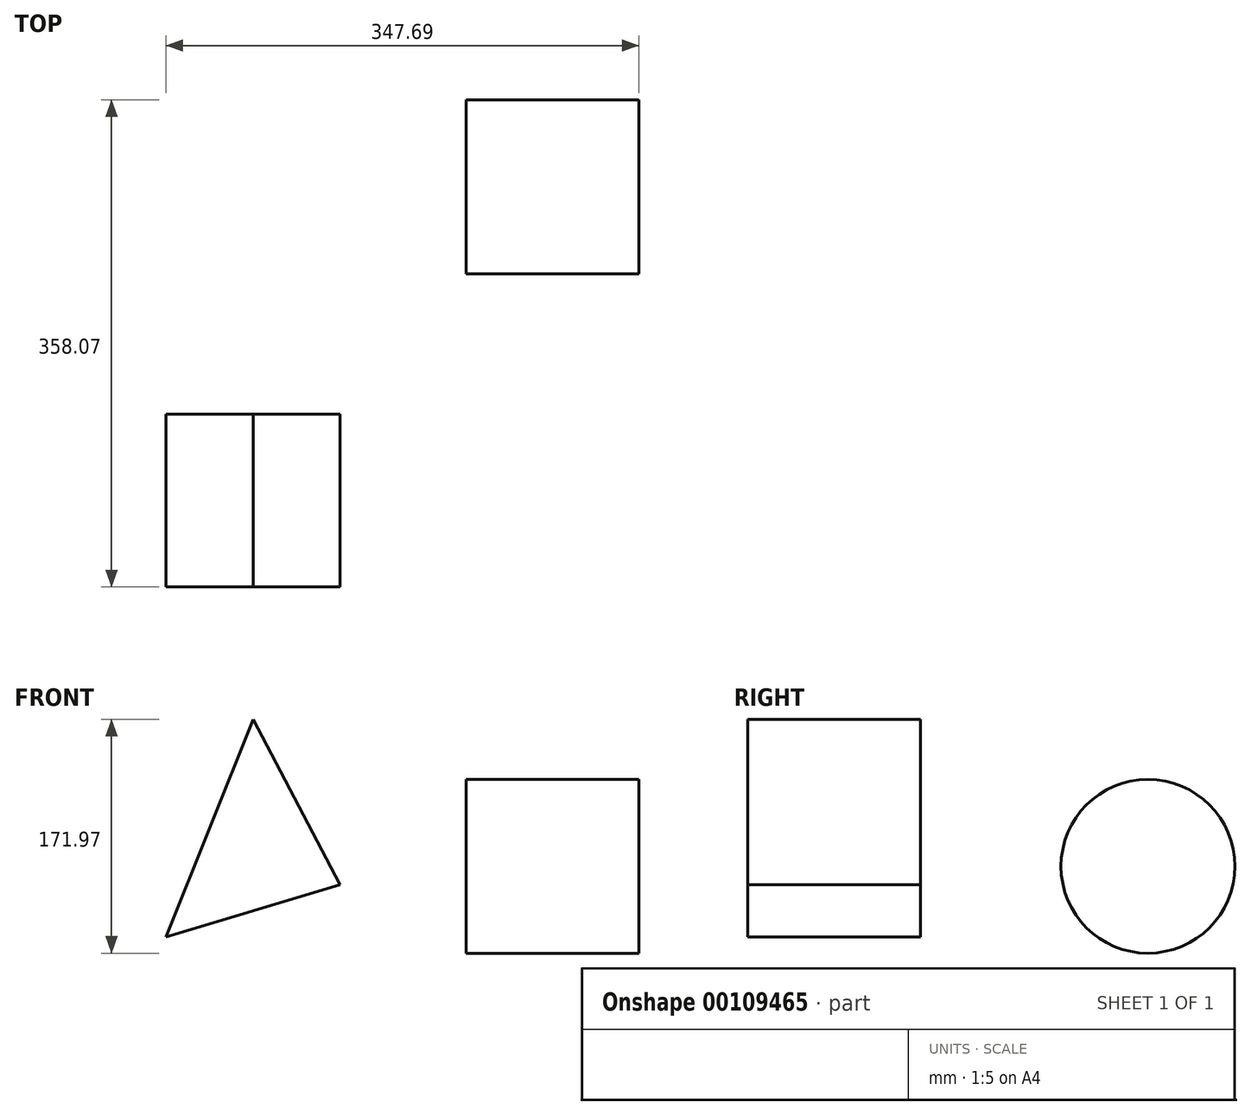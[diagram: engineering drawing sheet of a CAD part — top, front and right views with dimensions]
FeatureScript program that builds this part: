
annotation { "Feature Type Name" : "Feature", "Feature Type Description" : "" }
export const myFeature = defineFeature(function(context is Context, id is Id, definition is map)
    precondition{}
    {
        {
            var Q0;
            Q0=qCreatedBy(makeId("Front.planeOp"),FACE);
            var sketch = newSketch(context, id + "F0", { "sketchPlane" : qUnion([Q0])});
            skLineSegment(sketch, "E0", {"start": v(-220.7, -151.48) * mm, "end": v(-92.7, -112.83) * mm});
            skLineSegment(sketch, "E1", {"start": v(-220.7, -151.48) * mm, "end": v(-156.52, 8.63) * mm});
            skLineSegment(sketch, "E2", {"start": v(-156.52, 8.63) * mm, "end": v(-92.7, -112.83) * mm});
            skSolve(sketch);
        }
        {
            var Q0;
            Q0 = qSketchRegion(id + "F0", true);
            extrude(context, id + "F1", {"entities" : qUnion([Q0]), "depth" : 127 * mm});
        }
        {
            var Q0;
            Q0=qCreatedBy(makeId("Right.planeOp"),FACE);
            var sketch = newSketch(context, id + "F2", { "sketchPlane" : qUnion([Q0])});
            skCircle(sketch, "E3", {"center": v(167.19, -99.45) * mm, "radius": 63.89 * mm});
            skSolve(sketch);
        }
        {
            var Q0;
            Q0 = qSketchRegion(id + "F2", true);
            extrude(context, id + "F3", {"entities" : qUnion([Q0]), "depth" : 127 * mm});
        }
    });
